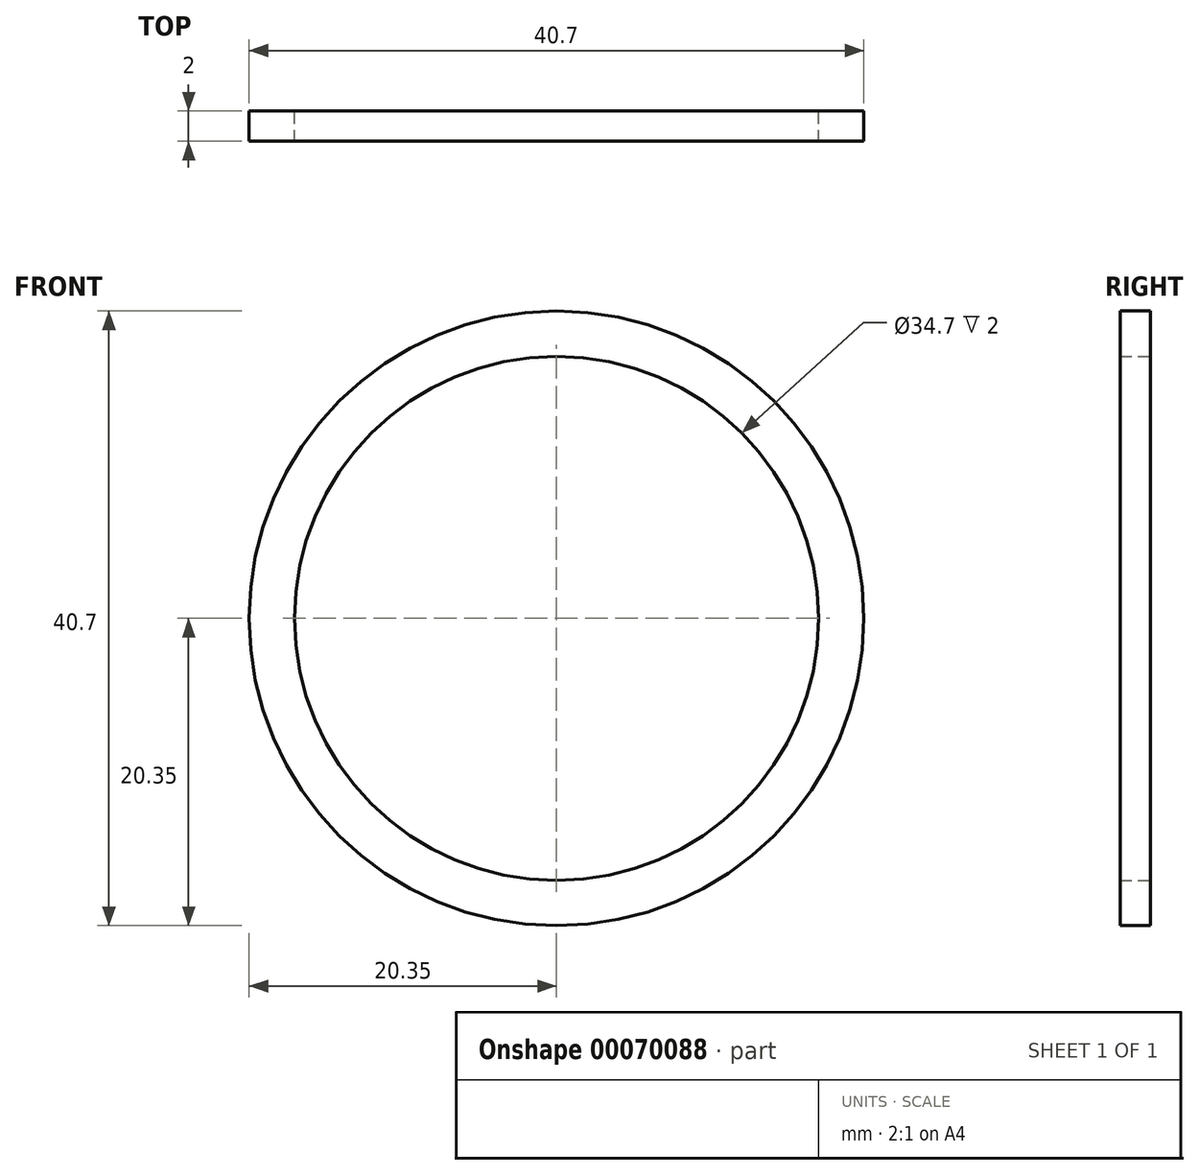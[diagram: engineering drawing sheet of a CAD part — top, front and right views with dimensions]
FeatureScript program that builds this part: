
annotation { "Feature Type Name" : "Feature", "Feature Type Description" : "" }
export const myFeature = defineFeature(function(context is Context, id is Id, definition is map)
    precondition{}
    {
        {
            var Q0;
            Q0=qCreatedBy(makeId("Front.planeOp"),FACE);
            var sketch = newSketch(context, id + "F0", { "sketchPlane" : qUnion([Q0])});
            skCircle(sketch, "E0", {"center": v(0, 0) * mm, "radius": 17.35 * mm});
            skCircle(sketch, "E1", {"center": v(0, 0) * mm, "radius": 20.35 * mm});
            skSolve(sketch);
        }
        {
            var Q0;
            Q0=qSketchRegion(id+"F0",true);
            extrude(context, id + "F1", {"entities" : qUnion([Q0]), "depth" : 2 * mm});
        }
    });
